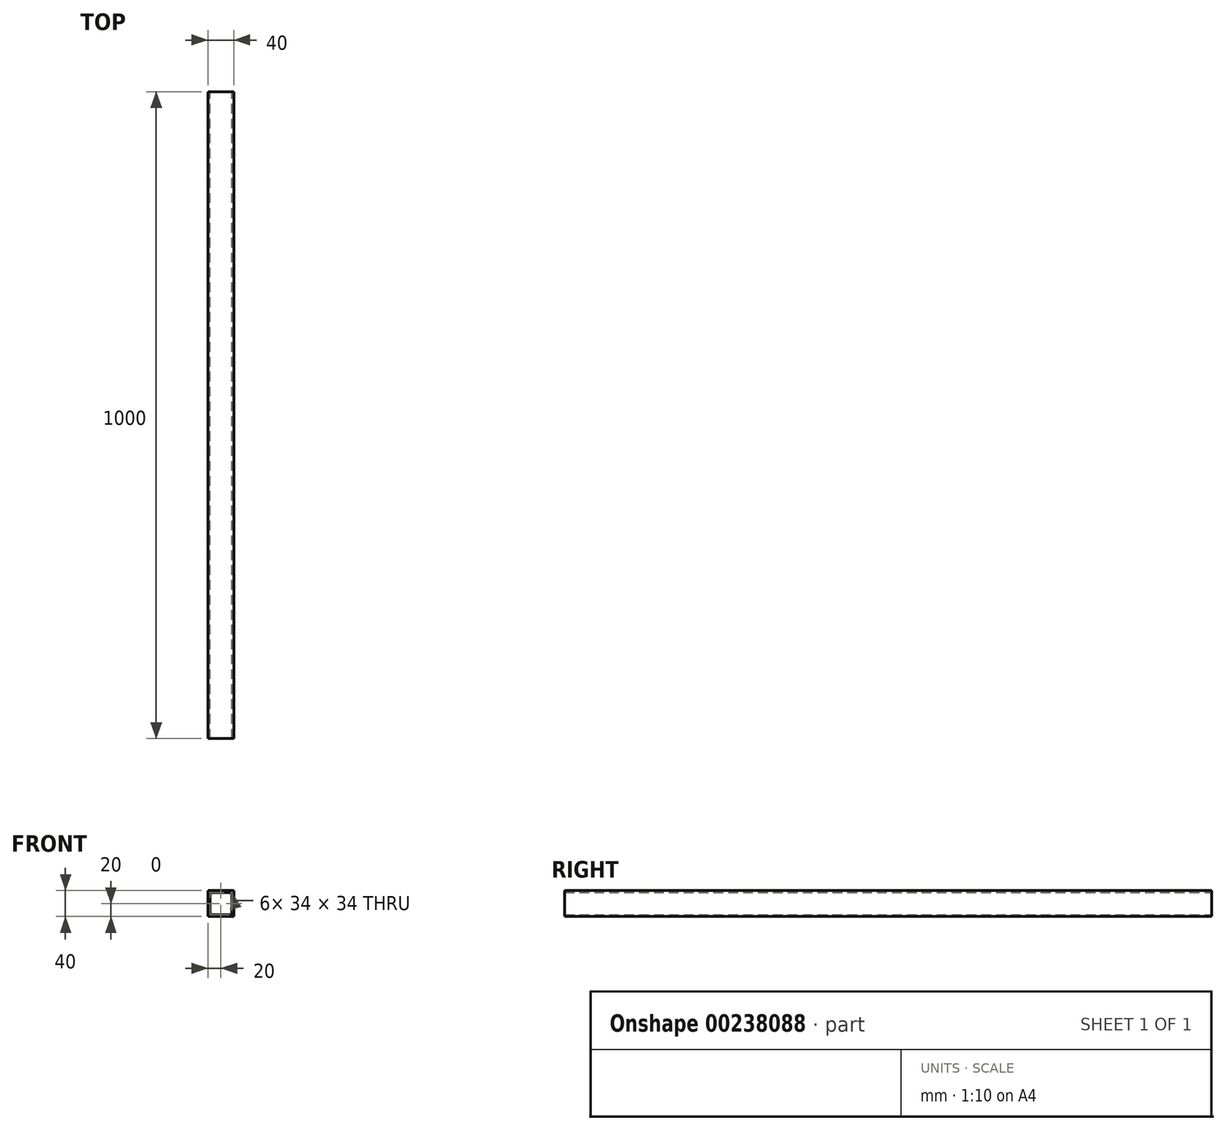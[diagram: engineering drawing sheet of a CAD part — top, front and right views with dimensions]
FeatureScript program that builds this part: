
annotation { "Feature Type Name" : "Feature", "Feature Type Description" : "" }
export const myFeature = defineFeature(function(context is Context, id is Id, definition is map)
    precondition{}
    {
        {
            var Q0;
            Q0=qCreatedBy(makeId("Front.planeOp"),FACE);
            var sketch = newSketch(context, id + "F0", { "sketchPlane" : qUnion([Q0])});
            skLineSegment(sketch, "E0.bottom", {"start": v(-20, 20) * mm, "end": v(20, 20) * mm});
            skLineSegment(sketch, "E0.top", {"start": v(-20, -20) * mm, "end": v(20, -20) * mm});
            skLineSegment(sketch, "E0.left", {"start": v(-20, 20) * mm, "end": v(-20, -20) * mm});
            skLineSegment(sketch, "E0.right", {"start": v(20, 20) * mm, "end": v(20, -20) * mm});
            skPoint(sketch, "E0.middle", {"position": v(0, 0) * mm});
            skLineSegment(sketch, "E1.bottom", {"start": v(17, 17) * mm, "end": v(-17, 17) * mm});
            skLineSegment(sketch, "E1.top", {"start": v(17, -17) * mm, "end": v(-17, -17) * mm});
            skLineSegment(sketch, "E1.left", {"start": v(17, 17) * mm, "end": v(17, -17) * mm});
            skLineSegment(sketch, "E1.right", {"start": v(-17, 17) * mm, "end": v(-17, -17) * mm});
            skSolve(sketch);
        }
        {
            var Q0;
            Q0=makeQuery(id+"F0.imprint","IMPRINT",FACE,{"disambiguationData":[TD([[makeQuery(id+"F0.imprint","IMPRINT",EDGE,{"derivedFrom":sQuery(id+"F0.wireOp",EDGE,"E0.bottom")}),-1.0]])]});
            extrude(context, id + "F1", {"entities" : qUnion([Q0]), "depth" : 1000 * mm});
        }
    });
